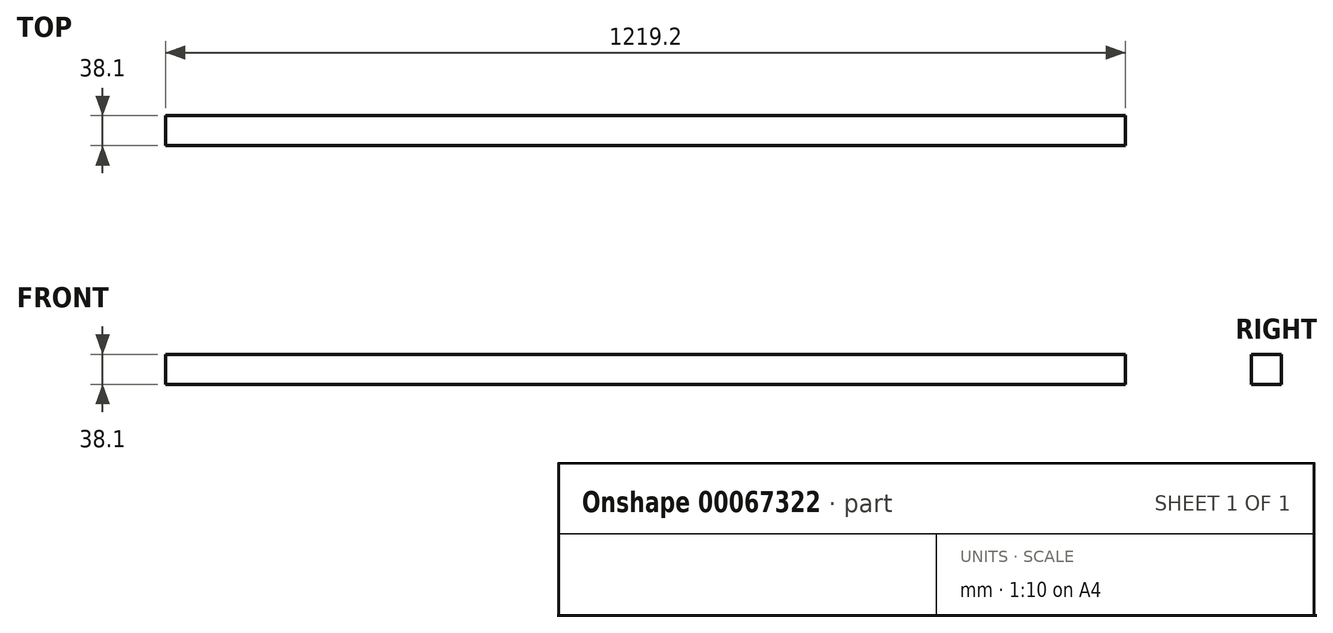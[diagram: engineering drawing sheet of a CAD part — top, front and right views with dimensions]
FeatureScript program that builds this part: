
annotation { "Feature Type Name" : "Feature", "Feature Type Description" : "" }
export const myFeature = defineFeature(function(context is Context, id is Id, definition is map)
    precondition{}
    {
        {
            var Q0;
            Q0=qCreatedBy(makeId("Top.planeOp"),FACE);
            var sketch = newSketch(context, id + "F0", { "sketchPlane" : qUnion([Q0])});
            skLineSegment(sketch, "E0.bottom", {"start": v(-590.64, -155.82) * mm, "end": v(628.56, -155.82) * mm});
            skLineSegment(sketch, "E0.top", {"start": v(-590.64, -193.92) * mm, "end": v(628.56, -193.92) * mm});
            skLineSegment(sketch, "E0.left", {"start": v(-590.64, -155.82) * mm, "end": v(-590.64, -193.92) * mm});
            skLineSegment(sketch, "E0.right", {"start": v(628.56, -155.82) * mm, "end": v(628.56, -193.92) * mm});
            skSolve(sketch);
        }
        {
            var Q0;
            Q0=makeQuery(id+"F0.imprint","IMPRINT",FACE,{"disambiguationData":[TD([[makeQuery(id+"F0.imprint","IMPRINT",EDGE,{"derivedFrom":sQuery(id+"F0.wireOp",EDGE,"E0.bottom")}),-1.0]])]});
            extrude(context, id + "F1", {"entities" : qUnion([Q0]), "depth" : 38.1 * mm});
        }
    });
